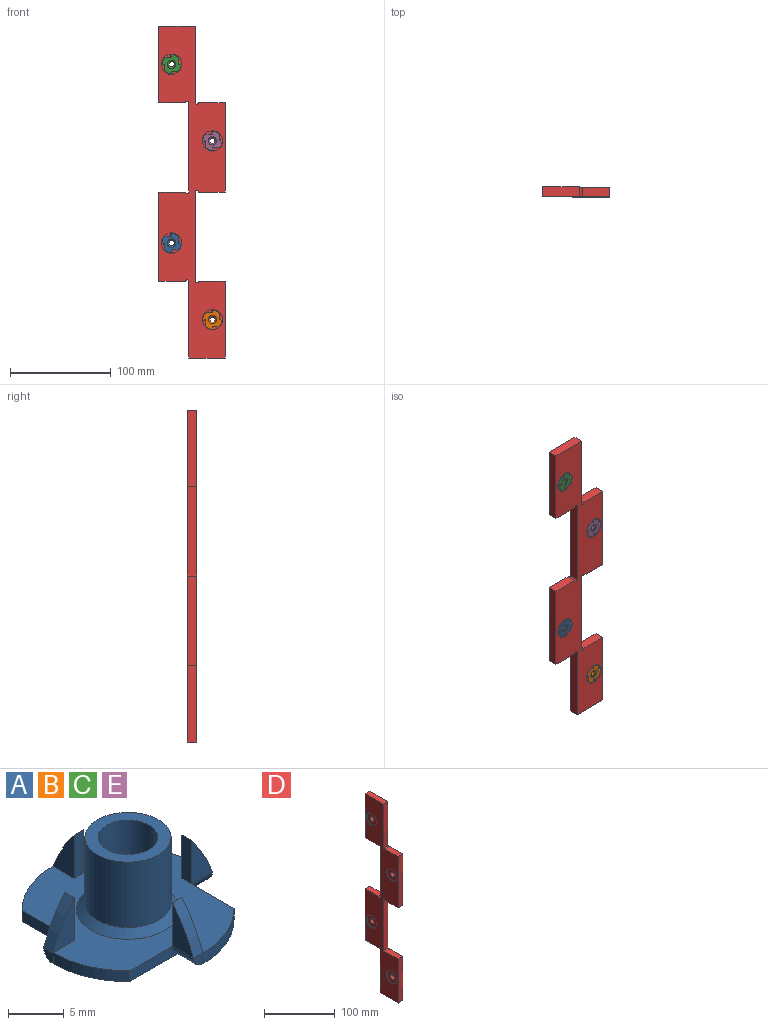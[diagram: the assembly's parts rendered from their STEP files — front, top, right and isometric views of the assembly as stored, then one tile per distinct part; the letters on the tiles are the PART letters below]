
ASSEMBLY  parts=5 mates=4
PART A: 39 faces, bbox 19.1x19.1x9.1 mm
  f0: cylinder r=9.53mm len=6.86mm, axis (0,0,-1), area 9.1mm2, adj f7,f10,f26,f28
  f1: cylinder r=16.73mm len=4.76mm, axis (0,-1,0), area 6.5mm2, adj f2,f3,f5,f6
  f2: plane 1.19x1.19mm, normal (1,0,0), area 1.1mm2, adj f1,f4,f27
  f3: plane 4.76x2.67mm, normal (0,-1,0), area 7.2mm2, adj f1,f4,f6
  f4: cylinder r=1.19mm len=2.67mm, axis (-1,0,0), area 5mm2, adj f2,f3,f7,f26
  f5: plane 4.76x2.67mm, normal (0,1,0), area 7.2mm2, adj f1,f6,f28
  f6: plane 4.76x1.19mm, normal (-1,0,0), area 5.7mm2, adj f1,f3,f5,f28
  f7: plane 6.61x1.19mm, normal (1,0,0), area 6.8mm2, adj f0,f4,f26,f28
  f8: cylinder r=9.53mm len=6.86mm, axis (0,0,-1), area 9.1mm2, adj f15,f18,f26,f28
  f9: cylinder r=16.73mm len=4.76mm, axis (-1,0,0), area 6.5mm2, adj f10,f11,f13,f14
  f10: plane 1.19x1.19mm, normal (0,-1,0), area 1.1mm2, adj f0,f9,f12
  f11: plane 4.76x2.67mm, normal (-1,0,0), area 7.2mm2, adj f9,f12,f14
  f12: cylinder r=1.19mm len=2.67mm, axis (0,1,0), area 5mm2, adj f10,f11,f15,f26
  f13: plane 4.76x2.67mm, normal (1,0,0), area 7.2mm2, adj f9,f14,f28
  f14: plane 4.76x1.19mm, normal (0,1,0), area 5.7mm2, adj f9,f11,f13,f28
  f15: plane 6.61x1.19mm, normal (0,-1,0), area 6.8mm2, adj f8,f12,f26,f28
  f16: cylinder r=9.53mm len=6.86mm, axis (0,0,-1), area 9.1mm2, adj f23,f26,f28,f34
  f17: cylinder r=16.73mm len=4.76mm, axis (0,1,0), area 6.5mm2, adj f18,f19,f21,f22
  f18: plane 1.19x1.19mm, normal (-1,0,0), area 1.1mm2, adj f8,f17,f20
  f19: plane 4.76x2.67mm, normal (0,1,0), area 7.2mm2, adj f17,f20,f22
  f20: cylinder r=1.19mm len=2.67mm, axis (1,0,0), area 5mm2, adj f18,f19,f23,f26
  f21: plane 4.76x2.67mm, normal (0,-1,0), area 7.2mm2, adj f17,f22,f28
  f22: plane 4.76x1.19mm, normal (1,0,0), area 5.7mm2, adj f17,f19,f21,f28
  f23: plane 6.61x1.19mm, normal (-1,0,0), area 6.8mm2, adj f16,f20,f26,f28
  f24: plane 4.76x2.67mm, normal (-1,0,0), area 7.2mm2, adj f28,f37,f38
  f25: cone r=2.68mm half-angle=45deg, axis (0,0,-1), area 44.3mm2, adj f26,f32
  f26: plane 19.05x19.05mm, normal (0,0,-1), area 182.6mm2, adj f0,f4,f7,f8,f12,f15,f16,f20
  f27: cylinder r=9.53mm len=6.86mm, axis (0,0,-1), area 9.1mm2, adj f2,f26,f28,f33
  f28: plane 19.05x19.05mm, normal (0,0,1), area 169mm2, adj f0,f5,f6,f7,f8,f13,f14,f15
  f29: cone r=4.64mm half-angle=45deg, axis (0,0,-1), area 28.8mm2, adj f28,f30
  f30: cylinder r=3.87mm len=7.75mm, axis (0,0,-1), area 174.9mm2, adj f29,f31
  f31: plane 7.75x7.75mm, normal (0,0,1), area 24.6mm2, adj f30,f32
  f32: cylinder r=2.68mm len=7.68mm, axis (0,0,-1), area 129.4mm2, adj f25,f31
  f33: plane 6.61x1.19mm, normal (0,1,0), area 6.8mm2, adj f26,f27,f28,f36
  f34: plane 1.19x1.19mm, normal (0,1,0), area 1.1mm2, adj f16,f36,f38
  f35: plane 4.76x2.67mm, normal (1,0,0), area 7.2mm2, adj f36,f37,f38
  f36: cylinder r=1.19mm len=2.67mm, axis (0,-1,0), area 5mm2, adj f26,f33,f34,f35
  f37: plane 4.76x1.19mm, normal (0,-1,0), area 5.7mm2, adj f24,f28,f35,f38
  f38: cylinder r=16.73mm len=4.76mm, axis (1,0,0), area 6.5mm2, adj f24,f34,f35,f37
PART B: same geometry as A
PART C: same geometry as A
PART D: 36 faces, bbox 9.5x66x330.2 mm
  f0: plane 26.67x9.53mm, normal (0,0,-1), area 254mm2, adj f7,f16,f17,f32
  f1: plane 26.67x9.53mm, normal (0,0,-1), area 254mm2, adj f10,f16,f17,f30
  f2: plane 26.67x9.53mm, normal (0,0,1), area 254mm2, adj f13,f16,f17,f35
  f3: plane 26.67x9.53mm, normal (0,0,1), area 254mm2, adj f4,f16,f17,f31
  f4: plane 76.2x9.53mm, normal (0,-1,0), area 725.8mm2, adj f3,f5,f16,f17
  f5: plane 36.2x9.53mm, normal (0,0,-1), area 344.8mm2, adj f4,f6,f16,f17
  f6: plane 76.2x9.53mm, normal (0,1,0), area 725.8mm2, adj f5,f16,f17,f32
  f7: plane 88.9x9.53mm, normal (0,1,0), area 846.8mm2, adj f0,f8,f16,f17
  f8: plane 26.67x9.53mm, normal (0,0,1), area 254mm2, adj f7,f16,f17,f33
  f9: plane 88.9x9.53mm, normal (0,1,0), area 846.8mm2, adj f16,f17,f30,f33
  f10: plane 76.2x9.53mm, normal (0,1,0), area 725.8mm2, adj f1,f11,f16,f17
  f11: plane 36.2x9.53mm, normal (0,0,1), area 344.8mm2, adj f10,f12,f16,f17
  f12: plane 76.2x9.53mm, normal (0,-1,0), area 725.8mm2, adj f11,f16,f17,f35
  f13: plane 88.9x9.53mm, normal (0,-1,0), area 846.8mm2, adj f2,f14,f16,f17
  f14: plane 26.67x9.53mm, normal (0,0,-1), area 254mm2, adj f13,f16,f17,f34
  f15: plane 88.9x9.53mm, normal (0,-1,0), area 846.8mm2, adj f16,f17,f31,f34
  f16: plane 330.2x66.04mm, normal (1,0,0), area 11729.3mm2, adj f0,f1,f2,f3,f4,f5,f6,f7
  f17: plane 330.2x66.04mm, normal (-1,0,0), area 10630.7mm2, adj f0,f1,f2,f3,f4,f5,f6,f7
  f18: cylinder r=3.98mm len=8.26mm, axis (-1,0,0), area 206.2mm2, adj f16,f19
  f19: plane 20.32x20.32mm, normal (-1,0,0), area 274.7mm2, adj f18,f20
  f20: cylinder r=10.16mm len=20.32mm, axis (-1,0,0), area 81.1mm2, adj f17,f19
  f21: cylinder r=3.98mm len=8.26mm, axis (-1,0,0), area 206.2mm2, adj f16,f22
  f22: plane 20.32x20.32mm, normal (-1,0,0), area 274.7mm2, adj f21,f23
  f23: cylinder r=10.16mm len=20.32mm, axis (-1,0,0), area 81.1mm2, adj f17,f22
  f24: cylinder r=3.98mm len=8.26mm, axis (-1,0,0), area 206.2mm2, adj f16,f25
  f25: plane 20.32x20.32mm, normal (-1,0,0), area 274.7mm2, adj f24,f26
  f26: cylinder r=10.16mm len=20.32mm, axis (-1,0,0), area 81.1mm2, adj f17,f25
  f27: cylinder r=3.98mm len=8.26mm, axis (-1,0,0), area 206.2mm2, adj f16,f28
  f28: plane 20.32x20.32mm, normal (-1,0,0), area 274.7mm2, adj f27,f29
  f29: cylinder r=10.16mm len=20.32mm, axis (-1,0,0), area 81.1mm2, adj f17,f28
  f30: cylinder r=1.59mm len=9.53mm, axis (-1,0,0), area 47.5mm2, adj f1,f9,f16,f17
  f31: cylinder r=1.59mm len=9.53mm, axis (-1,0,0), area 47.5mm2, adj f3,f15,f16,f17
  f32: cylinder r=1.59mm len=9.53mm, axis (-1,0,0), area 47.5mm2, adj f0,f6,f16,f17
  f33: cylinder r=1.59mm len=9.53mm, axis (-1,0,0), area 47.5mm2, adj f8,f9,f16,f17
  f34: cylinder r=1.59mm len=9.53mm, axis (-1,0,0), area 47.5mm2, adj f14,f15,f16,f17
  f35: cylinder r=1.59mm len=9.53mm, axis (-1,0,0), area 47.5mm2, adj f2,f12,f16,f17
PART E: same geometry as A
PLACE A rot(axis=(-1,0,0),90deg) t=(258.03,120.55,-88.52)mm
PLACE B rot(axis=(-1,0,0),90deg) t=(298.67,120.55,-164.72)mm
PLACE C rot(axis=(-1,0,0),90deg) t=(258.03,120.55,89.28)mm
PLACE D rot(axis=(0,0,1),90deg) t=(278.35,120.48,-212.35)mm
PLACE E rot(axis=(-1,0,0),90deg) t=(298.67,120.55,13.08)mm
MATE fastened D.f21 <-> E.f0  axis (0,-1,0) through (298.67,121.75,13.08)mm
MATE fastened D.f24 <-> A.f0  axis (0,-1,0) through (258.03,121.75,-88.52)mm
MATE fastened B.f0 <-> D.f27  axis (0,1,0) through (298.67,121.75,-164.72)mm
MATE fastened D.f18 <-> C.f0  axis (0,-1,0) through (258.03,121.75,89.28)mm
